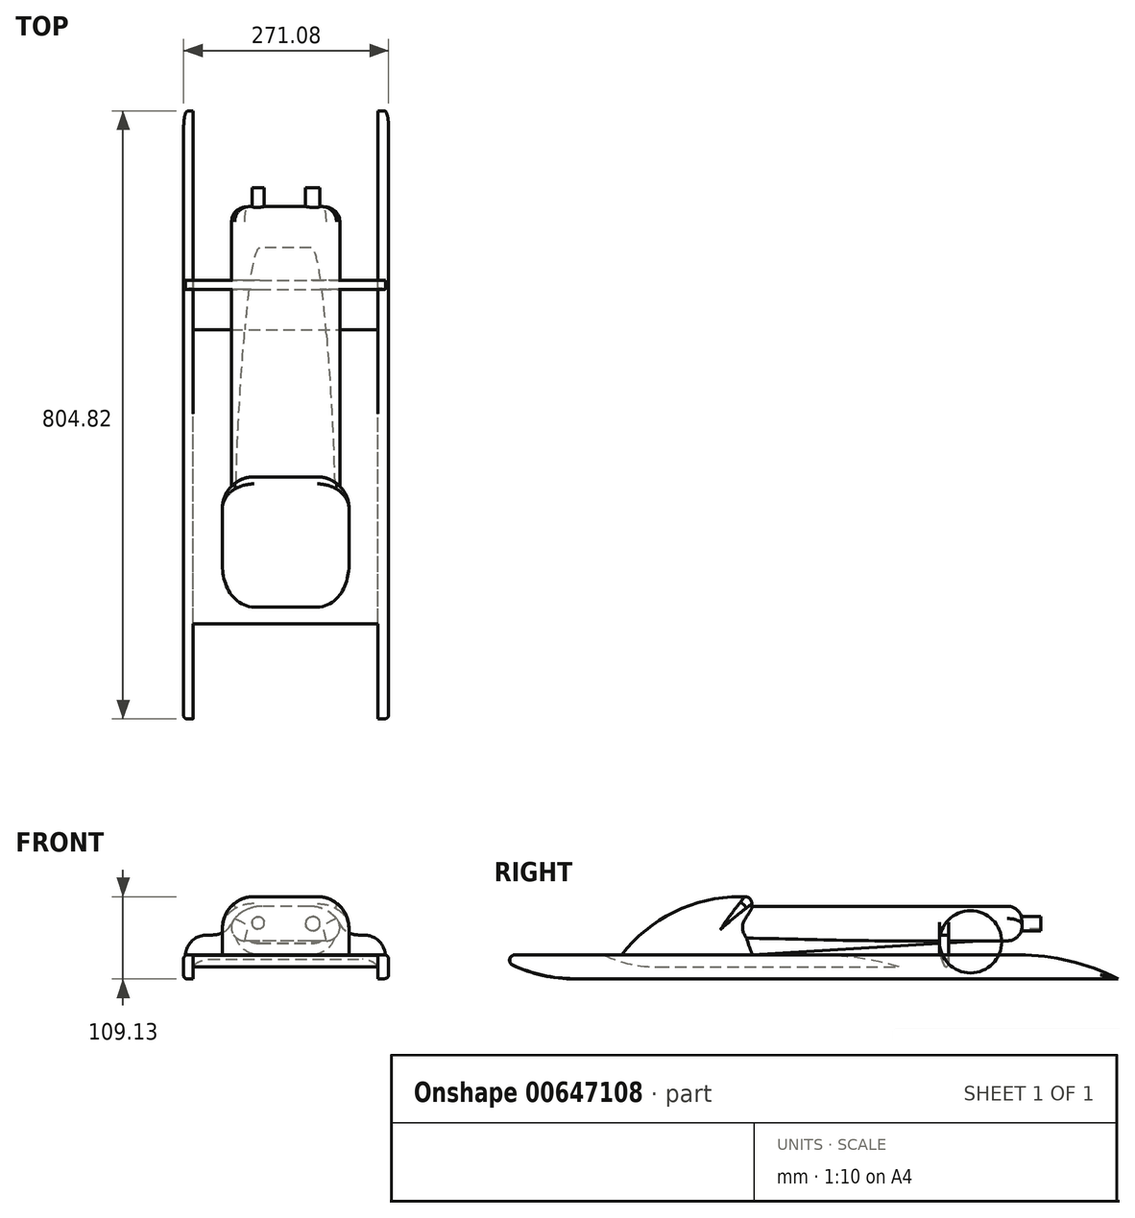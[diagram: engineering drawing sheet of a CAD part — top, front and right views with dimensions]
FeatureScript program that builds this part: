
annotation { "Feature Type Name" : "Feature", "Feature Type Description" : "" }
export const myFeature = defineFeature(function(context is Context, id is Id, definition is map)
    precondition{}
    {
        {
            var Q0;
            Q0=qCreatedBy(makeId("Front.planeOp"),FACE);
            var sketch = newSketch(context, id + "F0", { "sketchPlane" : qUnion([Q0])});
            skLineSegment(sketch, "E0.bottom", {"start": v(-123.74, 0) * mm, "end": v(124.22, 0) * mm});
            skLineSegment(sketch, "E0.top", {"start": v(-123.74, -15.94) * mm, "end": v(124.22, -15.94) * mm});
            skLineSegment(sketch, "E0.left", {"start": v(-123.74, 0) * mm, "end": v(-123.74, -15.94) * mm});
            skLineSegment(sketch, "E0.right", {"start": v(124.22, 0) * mm, "end": v(124.22, -15.94) * mm});
            skSolve(sketch);
        }
        {
            var Q0;
            Q0 = qSketchRegion(id + "F0", true);
            extrude(context, id + "F1", {"entities" : qUnion([Q0]), "endBound" : BoundingType.SYMMETRIC, "depth" : 389.65 * mm, "offsetDistance" : 25.4 * mm});
        }
        {
            var Q0;
            Q0=makeQuery(id+"F1.opExtrude","CAP_EDGE",EDGE,{"disambiguationData":[OSD([sQuery(id+"F0.wireOp",EDGE,"E0.bottom")])],"isStart":true});
            fillet(context, id + "F2", {"entities" : qUnion([Q0]), "radius" : 397.04 * mm, "tangentPropagation" : true, "allowEdgeOverflow" : false});
        }
        {
            var Q0;
            Q0=makeQuery(id+"F1.opExtrude","CAP_EDGE",EDGE,{"disambiguationData":[OSD([sQuery(id+"F0.wireOp",EDGE,"E0.top")])],"isStart":false});
            chamfer(context, id + "F3", {"entities" : qUnion([Q0]), "width" : 15.24 * mm, "tangentPropagation" : true});
        }
        {
            var Q0;
            {var subQ0=sQuery(id+"F0.wireOp",EDGE,"E0.top");Q0=makeQuery(id+"F3.opChamfer","BLEND_EDGE",EDGE,{"blendedFrom":[makeQuery(id+"F1.opExtrude","CAP_EDGE",EDGE,{"disambiguationData":[OSD([subQ0])],"isStart":false}),makeQuery(id+"F1.opExtrude","SWEPT_FACE",FACE,{"disambiguationData":[OSD([subQ0])]})],"blendedInto":[makeQuery(id+"F1.opExtrude","SWEPT_FACE",FACE,{"disambiguationData":[OSD([subQ0])]})]});}
            fillet(context, id + "F4", {"entities" : qUnion([Q0]), "radius" : 170.5 * mm, "tangentPropagation" : true, "allowEdgeOverflow" : false});
        }
        {
            var Q0;
            Q0=qCreatedBy(makeId("Front.planeOp"),FACE);
            var sketch = newSketch(context, id + "F5", { "sketchPlane" : qUnion([Q0])});
            skLineSegment(sketch, "E1.bottom", {"start": v(122.61, 0) * mm, "end": v(136.46, 0) * mm});
            skLineSegment(sketch, "E1.top", {"start": v(122.61, -31.37) * mm, "end": v(136.46, -31.37) * mm});
            skLineSegment(sketch, "E1.left", {"start": v(122.61, 0) * mm, "end": v(122.61, -31.37) * mm});
            skLineSegment(sketch, "E1.right", {"start": v(136.46, 0) * mm, "end": v(136.46, -31.37) * mm});
            skLineSegment(sketch, "E2.bottom", {"start": v(-122.4, 0) * mm, "end": v(-134.62, 0) * mm});
            skLineSegment(sketch, "E2.top", {"start": v(-122.4, -31.9) * mm, "end": v(-134.62, -31.9) * mm});
            skLineSegment(sketch, "E2.left", {"start": v(-122.4, 0) * mm, "end": v(-122.4, -31.9) * mm});
            skLineSegment(sketch, "E2.right", {"start": v(-134.62, 0) * mm, "end": v(-134.62, -31.9) * mm});
            skSolve(sketch);
        }
        {
            var Q0;
            Q0 = qSketchRegion(id + "F5", true);
            extrude(context, id + "F6", {"entities" : qUnion([Q0]), "operationType" : NewBodyOperationType.ADD, "endBound" : BoundingType.SYMMETRIC, "depth" : 680.15 * mm, "offsetDistance" : 25.4 * mm});
        }
        {
            var Q0;
            Q0=makeQuery(id+"F6.opExtrude","CAP_EDGE",EDGE,{"disambiguationData":[OSD([sQuery(id+"F5.wireOp",EDGE,"E1.top")])],"isStart":false});
            var Q1;
            Q1=makeQuery(id+"F6.opExtrude","CAP_EDGE",EDGE,{"disambiguationData":[OSD([sQuery(id+"F5.wireOp",EDGE,"E2.top")])],"isStart":false});
            fillet(context, id + "F7", {"entities" : qUnion([Q0, Q1]), "radius" : 190.44 * mm, "tangentPropagation" : true, "allowEdgeOverflow" : false});
        }
        {
            var Q0;
            Q0=makeQuery(id+"F6.opExtrude","CAP_FACE",FACE,{"disambiguationData":[OSD([sQuery(id+"F5.wireOp",EDGE,"E2.bottom"),sQuery(id+"F5.wireOp",EDGE,"E2.top"),sQuery(id+"F5.wireOp",EDGE,"E2.left"),sQuery(id+"F5.wireOp",EDGE,"E2.right")])],"isStart":true});
            var Q1;
            Q1=makeQuery(id+"F6.opExtrude","CAP_FACE",FACE,{"disambiguationData":[OSD([sQuery(id+"F5.wireOp",EDGE,"E1.bottom"),sQuery(id+"F5.wireOp",EDGE,"E1.top"),sQuery(id+"F5.wireOp",EDGE,"E1.left"),sQuery(id+"F5.wireOp",EDGE,"E1.right")])],"isStart":true});
            extrude(context, id + "F8", {"entities" : qUnion([Q0, Q1]), "operationType" : NewBodyOperationType.ADD, "depth" : 144.15 * mm, "offsetDistance" : 25.4 * mm});
        }
        {
            var Q0;
            Q0=makeQuery(id+"F8.opExtrude","CAP_EDGE",EDGE,{"disambiguationData":[OSD([sQuery(id+"F5.wireOp",EDGE,"E2.bottom")])],"isStart":false});
            var Q1;
            Q1=makeQuery(id+"F8.opExtrude","CAP_EDGE",EDGE,{"disambiguationData":[OSD([sQuery(id+"F5.wireOp",EDGE,"E1.bottom")])],"isStart":false});
            fillet(context, id + "F9", {"entities" : qUnion([Q0, Q1]), "radius" : 288.6 * mm, "tangentPropagation" : true, "allowEdgeOverflow" : false});
        }
        {
            var Q0;
            Q0=qCreatedBy(makeId("Front.planeOp"),FACE);
            var sketch = newSketch(context, id + "F10", { "sketchPlane" : qUnion([Q0])});
            skLineSegment(sketch, "E3.bottom", {"start": v(-83.53, 0) * mm, "end": v(84.18, 0) * mm});
            skLineSegment(sketch, "E3.top", {"start": v(-83.53, 77.23) * mm, "end": v(84.18, 77.23) * mm});
            skLineSegment(sketch, "E3.left", {"start": v(-83.53, 0) * mm, "end": v(-83.53, 77.23) * mm});
            skLineSegment(sketch, "E3.right", {"start": v(84.18, 0) * mm, "end": v(84.18, 77.23) * mm});
            skSolve(sketch);
        }
        {
            var Q0;
            Q0 = qSketchRegion(id + "F10", true);
            extrude(context, id + "F11", {"entities" : qUnion([Q0]), "operationType" : NewBodyOperationType.ADD, "depth" : 172.3 * mm, "offsetDistance" : 25.4 * mm});
        }
        {
            var Q0;
            Q0=makeQuery(id+"F11.opExtrude","CAP_EDGE",EDGE,{"disambiguationData":[OSD([sQuery(id+"F10.wireOp",EDGE,"E3.top")])],"isStart":false});
            fillet(context, id + "F12", {"entities" : qUnion([Q0]), "radius" : 198.08 * mm, "tangentPropagation" : true, "allowEdgeOverflow" : false});
        }
        {
            var Q0;
            Q0=makeQuery(id+"F11.opExtrude","CAP_EDGE",EDGE,{"disambiguationData":[OSD([sQuery(id+"F10.wireOp",EDGE,"E3.top")])],"isStart":true});
            fillet(context, id + "F13", {"entities" : qUnion([Q0]), "radius" : 9.37 * mm, "tangentPropagation" : true, "allowEdgeOverflow" : false});
        }
        {
            var Q0;
            Q0=makeQuery(id+"F7.opFillet","BLEND_EDGE",EDGE,{"blendedFrom":[makeQuery(id+"F6.opExtrude","CAP_EDGE",EDGE,{"disambiguationData":[OSD([sQuery(id+"F5.wireOp",EDGE,"E2.top")])],"isStart":false}),makeQuery(id+"F6.boolean.opBoolean","MERGE",FACE,{"derivedFrom":[makeQuery(id+"F1.opExtrude","SWEPT_FACE",FACE,{"disambiguationData":[OSD([sQuery(id+"F0.wireOp",EDGE,"E0.bottom")])]}),makeQuery(id+"F6.opExtrude","SWEPT_FACE",FACE,{"disambiguationData":[OSD([sQuery(id+"F5.wireOp",EDGE,"E1.bottom")])]}),makeQuery(id+"F6.opExtrude","SWEPT_FACE",FACE,{"disambiguationData":[OSD([sQuery(id+"F5.wireOp",EDGE,"E2.bottom")])]})]})],"blendedInto":[makeQuery(id+"F6.boolean.opBoolean","MERGE",FACE,{"derivedFrom":[makeQuery(id+"F1.opExtrude","SWEPT_FACE",FACE,{"disambiguationData":[OSD([sQuery(id+"F0.wireOp",EDGE,"E0.bottom")])]}),makeQuery(id+"F6.opExtrude","SWEPT_FACE",FACE,{"disambiguationData":[OSD([sQuery(id+"F5.wireOp",EDGE,"E1.bottom")])]}),makeQuery(id+"F6.opExtrude","SWEPT_FACE",FACE,{"disambiguationData":[OSD([sQuery(id+"F5.wireOp",EDGE,"E2.bottom")])]})]})]});
            var Q1;
            Q1=makeQuery(id+"F7.opFillet","BLEND_EDGE",EDGE,{"blendedFrom":[makeQuery(id+"F6.opExtrude","CAP_EDGE",EDGE,{"disambiguationData":[OSD([sQuery(id+"F5.wireOp",EDGE,"E1.top")])],"isStart":false}),makeQuery(id+"F6.boolean.opBoolean","MERGE",FACE,{"derivedFrom":[makeQuery(id+"F1.opExtrude","SWEPT_FACE",FACE,{"disambiguationData":[OSD([sQuery(id+"F0.wireOp",EDGE,"E0.bottom")])]}),makeQuery(id+"F6.opExtrude","SWEPT_FACE",FACE,{"disambiguationData":[OSD([sQuery(id+"F5.wireOp",EDGE,"E1.bottom")])]}),makeQuery(id+"F6.opExtrude","SWEPT_FACE",FACE,{"disambiguationData":[OSD([sQuery(id+"F5.wireOp",EDGE,"E2.bottom")])]})]})],"blendedInto":[makeQuery(id+"F6.boolean.opBoolean","MERGE",FACE,{"derivedFrom":[makeQuery(id+"F1.opExtrude","SWEPT_FACE",FACE,{"disambiguationData":[OSD([sQuery(id+"F0.wireOp",EDGE,"E0.bottom")])]}),makeQuery(id+"F6.opExtrude","SWEPT_FACE",FACE,{"disambiguationData":[OSD([sQuery(id+"F5.wireOp",EDGE,"E1.bottom")])]}),makeQuery(id+"F6.opExtrude","SWEPT_FACE",FACE,{"disambiguationData":[OSD([sQuery(id+"F5.wireOp",EDGE,"E2.bottom")])]})]})]});
            fillet(context, id + "F14", {"entities" : qUnion([Q0, Q1]), "radius" : 7 * mm, "tangentPropagation" : true, "allowEdgeOverflow" : false});
        }
        {
            var Q0;
            Q0=qCreatedBy(makeId("Front.planeOp"),FACE);
            var sketch = newSketch(context, id + "F15", { "sketchPlane" : qUnion([Q0])});
            skLineSegment(sketch, "E4.bottom", {"start": v(79.44, 64.47) * mm, "end": v(-78.92, 64.47) * mm});
            skLineSegment(sketch, "E4.top", {"start": v(79.44, 18.65) * mm, "end": v(-78.92, 18.65) * mm});
            skLineSegment(sketch, "E4.left", {"start": v(79.44, 64.47) * mm, "end": v(79.44, 18.65) * mm});
            skLineSegment(sketch, "E4.right", {"start": v(-78.92, 64.47) * mm, "end": v(-78.92, 18.65) * mm});
            skSolve(sketch);
        }
        {
            var Q0;
            Q0 = qSketchRegion(id + "F15", true);
            extrude(context, id + "F16", {"entities" : qUnion([Q0]), "operationType" : NewBodyOperationType.ADD, "oppositeDirection" : true, "depth" : 357.55 * mm, "offsetDistance" : 25.4 * mm});
        }
        {
            var Q0;
            Q0=qCreatedBy(makeId("Right.planeOp"),FACE);
            var sketch = newSketch(context, id + "F17", { "sketchPlane" : qUnion([Q0])});
            skLineSegment(sketch, "E5", {"start": v(350.7, 21.59) * mm, "end": v(0, 0) * mm});
            skLineSegment(sketch, "E6", {"start": v(0, 0) * mm, "end": v(-0.17, 23.5) * mm});
            skLineSegment(sketch, "E7", {"start": v(-0.17, 23.5) * mm, "end": v(350.7, 21.59) * mm});
            skSolve(sketch);
        }
        {
            var Q0;
            Q0=makeQuery(id+"F17.imprint","IMPRINT",FACE,{"disambiguationData":[TD([[makeQuery(id+"F17.imprint","IMPRINT",EDGE,{"derivedFrom":sQuery(id+"F17.wireOp",EDGE,"E5")}),-1.0]])]});
            extrude(context, id + "F18", {"entities" : qUnion([Q0]), "operationType" : NewBodyOperationType.ADD, "endBound" : BoundingType.SYMMETRIC, "depth" : 133.14 * mm, "offsetDistance" : 25.4 * mm});
        }
        {
            var Q0;
            Q0=makeQuery(id+"F18.opExtrude","CAP_EDGE",EDGE,{"disambiguationData":[OSD([sQuery(id+"F17.wireOp",EDGE,"E5")])],"isStart":false});
            var Q1;
            Q1=makeQuery(id+"F18.opExtrude","CAP_EDGE",EDGE,{"disambiguationData":[OSD([sQuery(id+"F17.wireOp",EDGE,"E5")])],"isStart":true});
            fillet(context, id + "F19", {"entities" : qUnion([Q0, Q1]), "radius" : 32.62 * mm, "tangentPropagation" : true, "allowEdgeOverflow" : false});
        }
        {
            var Q0;
            Q0=makeQuery(id+"F12.opFillet","BLEND_EDGE",EDGE,{"blendedFrom":[makeQuery(id+"F11.opExtrude","CAP_EDGE",EDGE,{"disambiguationData":[OSD([sQuery(id+"F10.wireOp",EDGE,"E3.top")])],"isStart":false}),makeQuery(id+"F11.opExtrude","SWEPT_FACE",FACE,{"disambiguationData":[OSD([sQuery(id+"F10.wireOp",EDGE,"E3.right")])]})],"blendedInto":[makeQuery(id+"F11.opExtrude","SWEPT_FACE",FACE,{"disambiguationData":[OSD([sQuery(id+"F10.wireOp",EDGE,"E3.right")])]})]});
            var Q1;
            Q1=makeQuery(id+"F12.opFillet","BLEND_EDGE",EDGE,{"blendedFrom":[makeQuery(id+"F11.opExtrude","CAP_EDGE",EDGE,{"disambiguationData":[OSD([sQuery(id+"F10.wireOp",EDGE,"E3.top")])],"isStart":false}),makeQuery(id+"F11.opExtrude","SWEPT_FACE",FACE,{"disambiguationData":[OSD([sQuery(id+"F10.wireOp",EDGE,"E3.left")])]})],"blendedInto":[makeQuery(id+"F11.opExtrude","SWEPT_FACE",FACE,{"disambiguationData":[OSD([sQuery(id+"F10.wireOp",EDGE,"E3.left")])]})]});
            fillet(context, id + "F20", {"entities" : qUnion([Q0, Q1]), "radius" : 42.05 * mm, "tangentPropagation" : true, "allowEdgeOverflow" : false});
        }
        {
            var Q0;
            Q0=makeQuery(id+"F16.opExtrude","SWEPT_EDGE",EDGE,{"disambiguationData":[OSD([sQuery(id+"F15.wireOp",EDGE,"E4.bottom"),sQuery(id+"F15.wireOp",EDGE,"E4.right")])]});
            var Q1;
            Q1=makeQuery(id+"F16.opExtrude","SWEPT_EDGE",EDGE,{"disambiguationData":[OSD([sQuery(id+"F15.wireOp",EDGE,"E4.bottom"),sQuery(id+"F15.wireOp",EDGE,"E4.left")])]});
            fillet(context, id + "F21", {"entities" : qUnion([Q0, Q1]), "radius" : 48.04 * mm, "tangentPropagation" : true, "allowEdgeOverflow" : false});
        }
        {
            var Q0;
            Q0=makeQuery(id+"F21.opFillet","BLEND_EDGE",EDGE,{"blendedFrom":[makeQuery(id+"F16.opExtrude","SWEPT_EDGE",EDGE,{"disambiguationData":[OSD([sQuery(id+"F15.wireOp",EDGE,"E4.bottom"),sQuery(id+"F15.wireOp",EDGE,"E4.left")])]}),makeQuery(id+"F16.opExtrude","SWEPT_FACE",FACE,{"disambiguationData":[OSD([sQuery(id+"F15.wireOp",EDGE,"E4.top")])]})],"blendedInto":[makeQuery(id+"F16.opExtrude","SWEPT_FACE",FACE,{"disambiguationData":[OSD([sQuery(id+"F15.wireOp",EDGE,"E4.top")])]})]});
            var Q1;
            Q1=makeQuery(id+"F21.opFillet","BLEND_EDGE",EDGE,{"blendedFrom":[makeQuery(id+"F16.opExtrude","SWEPT_EDGE",EDGE,{"disambiguationData":[OSD([sQuery(id+"F15.wireOp",EDGE,"E4.bottom"),sQuery(id+"F15.wireOp",EDGE,"E4.right")])]}),makeQuery(id+"F16.opExtrude","SWEPT_FACE",FACE,{"disambiguationData":[OSD([sQuery(id+"F15.wireOp",EDGE,"E4.top")])]})],"blendedInto":[makeQuery(id+"F16.opExtrude","SWEPT_FACE",FACE,{"disambiguationData":[OSD([sQuery(id+"F15.wireOp",EDGE,"E4.top")])]})]});
            fillet(context, id + "F22", {"entities" : qUnion([Q0, Q1]), "radius" : 17.76 * mm, "tangentPropagation" : true, "allowEdgeOverflow" : false});
        }
        {
            var Q0;
            Q0=makeQuery(id+"F16.opExtrude","CAP_FACE",FACE,{"disambiguationData":[OSD([sQuery(id+"F15.wireOp",EDGE,"E4.bottom"),sQuery(id+"F15.wireOp",EDGE,"E4.top"),sQuery(id+"F15.wireOp",EDGE,"E4.left"),sQuery(id+"F15.wireOp",EDGE,"E4.right")])],"isStart":false});
            fillet(context, id + "F23", {"entities" : qUnion([Q0]), "radius" : 19.7 * mm, "tangentPropagation" : true, "allowEdgeOverflow" : false});
        }
        {
            var Q0;
            Q0=qCreatedBy(makeId("Right.planeOp"),FACE);
            var sketch = newSketch(context, id + "F24", { "sketchPlane" : qUnion([Q0])});
            skLineSegment(sketch, "E8.bottom", {"start": v(260.18, 26.41) * mm, "end": v(248.12, 26.41) * mm});
            skLineSegment(sketch, "E8.top", {"start": v(260.18, -11.71) * mm, "end": v(248.12, -11.71) * mm});
            skLineSegment(sketch, "E8.left", {"start": v(260.18, 26.41) * mm, "end": v(260.18, -11.71) * mm});
            skLineSegment(sketch, "E8.right", {"start": v(248.12, 26.41) * mm, "end": v(248.12, -11.71) * mm});
            skSolve(sketch);
        }
        {
            var Q0;
            Q0 = qSketchRegion(id + "F24", true);
            extrude(context, id + "F25", {"entities" : qUnion([Q0]), "operationType" : NewBodyOperationType.ADD, "endBound" : BoundingType.SYMMETRIC, "depth" : 264.57 * mm, "offsetDistance" : 25.4 * mm});
        }
        {
            var Q0;
            Q0=makeQuery(id+"F25.opExtrude","CAP_EDGE",EDGE,{"disambiguationData":[OSD([sQuery(id+"F24.wireOp",EDGE,"E8.bottom")])],"isStart":true});
            var Q1;
            Q1=makeQuery(id+"F25.boolean.opBoolean","INTERSECT",EDGE,{"derivedFrom":[makeQuery(id+"F22.opFillet","BLEND_FACE",FACE,{"disambiguationData":[OSD([sQuery(id+"F15.wireOp",EDGE,"E4.bottom"),sQuery(id+"F15.wireOp",EDGE,"E4.top"),sQuery(id+"F15.wireOp",EDGE,"E4.right")])]}),makeQuery(id+"F25.opExtrude","SWEPT_FACE",FACE,{"disambiguationData":[OSD([sQuery(id+"F24.wireOp",EDGE,"E8.bottom")])]})]});
            var Q2;
            Q2=makeQuery(id+"F25.opExtrude","CAP_EDGE",EDGE,{"disambiguationData":[OSD([sQuery(id+"F24.wireOp",EDGE,"E8.bottom")])],"isStart":false});
            var Q3;
            Q3=makeQuery(id+"F25.boolean.opBoolean","INTERSECT",EDGE,{"derivedFrom":[makeQuery(id+"F22.opFillet","BLEND_FACE",FACE,{"disambiguationData":[OSD([sQuery(id+"F15.wireOp",EDGE,"E4.bottom"),sQuery(id+"F15.wireOp",EDGE,"E4.top"),sQuery(id+"F15.wireOp",EDGE,"E4.left")])]}),makeQuery(id+"F25.opExtrude","SWEPT_FACE",FACE,{"disambiguationData":[OSD([sQuery(id+"F24.wireOp",EDGE,"E8.bottom")])]})]});
            fillet(context, id + "F26", {"entities" : qUnion([Q0, Q1, Q2, Q3]), "radius" : 28.48 * mm, "tangentPropagation" : true, "allowEdgeOverflow" : false});
        }
        {
            var Q0;
            {var subQ0=sQuery(id+"F5.wireOp",EDGE,"E1.left");Q0=makeQuery(id+"F25.boolean.opBoolean","INTERSECT",EDGE,{"derivedFrom":[makeQuery(id+"F8.boolean.opBoolean","MERGE",FACE,{"derivedFrom":[makeQuery(id+"F6.opExtrude","SWEPT_FACE",FACE,{"disambiguationData":[OSD([subQ0])]}),makeQuery(id+"F8.opExtrude","SWEPT_FACE",FACE,{"disambiguationData":[OSD([subQ0])]})]}),makeQuery(id+"F25.opExtrude","SWEPT_FACE",FACE,{"disambiguationData":[OSD([sQuery(id+"F24.wireOp",EDGE,"E8.top")])]})]});}
            var Q1;
            {var subQ0=sQuery(id+"F5.wireOp",EDGE,"E2.left");Q1=makeQuery(id+"F25.boolean.opBoolean","INTERSECT",EDGE,{"derivedFrom":[makeQuery(id+"F8.boolean.opBoolean","MERGE",FACE,{"derivedFrom":[makeQuery(id+"F6.opExtrude","SWEPT_FACE",FACE,{"disambiguationData":[OSD([subQ0])]}),makeQuery(id+"F8.opExtrude","SWEPT_FACE",FACE,{"disambiguationData":[OSD([subQ0])]})]}),makeQuery(id+"F25.opExtrude","SWEPT_FACE",FACE,{"disambiguationData":[OSD([sQuery(id+"F24.wireOp",EDGE,"E8.top")])]})]});}
            fillet(context, id + "F27", {"entities" : qUnion([Q0, Q1]), "radius" : 20.53 * mm, "tangentPropagation" : true, "allowEdgeOverflow" : false});
        }
        {
            var Q0;
            {var subQ0=sQuery(id+"F5.wireOp",EDGE,"E2.left");Q0=makeQuery(id+"F27.opFillet","BLEND_EDGE",EDGE,{"blendedFrom":[makeQuery(id+"F25.boolean.opBoolean","INTERSECT",EDGE,{"derivedFrom":[makeQuery(id+"F8.boolean.opBoolean","MERGE",FACE,{"derivedFrom":[makeQuery(id+"F6.opExtrude","SWEPT_FACE",FACE,{"disambiguationData":[OSD([subQ0])]}),makeQuery(id+"F8.opExtrude","SWEPT_FACE",FACE,{"disambiguationData":[OSD([subQ0])]})]}),makeQuery(id+"F25.opExtrude","SWEPT_FACE",FACE,{"disambiguationData":[OSD([sQuery(id+"F24.wireOp",EDGE,"E8.top")])]})]}),makeQuery(id+"F25.opExtrude","SWEPT_FACE",FACE,{"disambiguationData":[OSD([sQuery(id+"F24.wireOp",EDGE,"E8.right")])]})],"blendedInto":[makeQuery(id+"F25.opExtrude","SWEPT_FACE",FACE,{"disambiguationData":[OSD([sQuery(id+"F24.wireOp",EDGE,"E8.right")])]})]});}
            var Q1;
            Q1=makeQuery(id+"F25.opExtrude","SWEPT_EDGE",EDGE,{"disambiguationData":[OSD([sQuery(id+"F24.wireOp",EDGE,"E8.top"),sQuery(id+"F24.wireOp",EDGE,"E8.right")])]});
            var Q2;
            {var subQ0=sQuery(id+"F5.wireOp",EDGE,"E1.left");Q2=makeQuery(id+"F27.opFillet","BLEND_EDGE",EDGE,{"blendedFrom":[makeQuery(id+"F25.boolean.opBoolean","INTERSECT",EDGE,{"derivedFrom":[makeQuery(id+"F8.boolean.opBoolean","MERGE",FACE,{"derivedFrom":[makeQuery(id+"F6.opExtrude","SWEPT_FACE",FACE,{"disambiguationData":[OSD([subQ0])]}),makeQuery(id+"F8.opExtrude","SWEPT_FACE",FACE,{"disambiguationData":[OSD([subQ0])]})]}),makeQuery(id+"F25.opExtrude","SWEPT_FACE",FACE,{"disambiguationData":[OSD([sQuery(id+"F24.wireOp",EDGE,"E8.top")])]})]}),makeQuery(id+"F25.opExtrude","SWEPT_FACE",FACE,{"disambiguationData":[OSD([sQuery(id+"F24.wireOp",EDGE,"E8.right")])]})],"blendedInto":[makeQuery(id+"F25.opExtrude","SWEPT_FACE",FACE,{"disambiguationData":[OSD([sQuery(id+"F24.wireOp",EDGE,"E8.right")])]})]});}
            fillet(context, id + "F28", {"entities" : qUnion([Q0, Q1, Q2]), "radius" : 41.19 * mm, "tangentPropagation" : true, "allowEdgeOverflow" : false});
        }
        {
            var Q0;
            Q0=makeQuery(id+"F28.opFillet","BLEND_EDGE",EDGE,{"blendedFrom":[makeQuery(id+"F25.opExtrude","SWEPT_EDGE",EDGE,{"disambiguationData":[OSD([sQuery(id+"F24.wireOp",EDGE,"E8.top"),sQuery(id+"F24.wireOp",EDGE,"E8.right")])]}),makeQuery(id+"F25.opExtrude","SWEPT_FACE",FACE,{"disambiguationData":[OSD([sQuery(id+"F24.wireOp",EDGE,"E8.left")])]})],"blendedInto":[makeQuery(id+"F25.opExtrude","SWEPT_FACE",FACE,{"disambiguationData":[OSD([sQuery(id+"F24.wireOp",EDGE,"E8.left")])]})]});
            var Q1;
            {var subQ0=sQuery(id+"F5.wireOp",EDGE,"E1.left");Q1=makeQuery(id+"F28.opFillet","BLEND_EDGE",EDGE,{"blendedFrom":[makeQuery(id+"F27.opFillet","BLEND_EDGE",EDGE,{"blendedFrom":[makeQuery(id+"F25.boolean.opBoolean","INTERSECT",EDGE,{"derivedFrom":[makeQuery(id+"F8.boolean.opBoolean","MERGE",FACE,{"derivedFrom":[makeQuery(id+"F6.opExtrude","SWEPT_FACE",FACE,{"disambiguationData":[OSD([subQ0])]}),makeQuery(id+"F8.opExtrude","SWEPT_FACE",FACE,{"disambiguationData":[OSD([subQ0])]})]}),makeQuery(id+"F25.opExtrude","SWEPT_FACE",FACE,{"disambiguationData":[OSD([sQuery(id+"F24.wireOp",EDGE,"E8.top")])]})]}),makeQuery(id+"F25.opExtrude","SWEPT_FACE",FACE,{"disambiguationData":[OSD([sQuery(id+"F24.wireOp",EDGE,"E8.right")])]})],"blendedInto":[makeQuery(id+"F25.opExtrude","SWEPT_FACE",FACE,{"disambiguationData":[OSD([sQuery(id+"F24.wireOp",EDGE,"E8.right")])]})]}),makeQuery(id+"F25.opExtrude","SWEPT_FACE",FACE,{"disambiguationData":[OSD([sQuery(id+"F24.wireOp",EDGE,"E8.left")])]})],"blendedInto":[makeQuery(id+"F25.opExtrude","SWEPT_FACE",FACE,{"disambiguationData":[OSD([sQuery(id+"F24.wireOp",EDGE,"E8.left")])]})]});}
            fillet(context, id + "F29", {"entities" : qUnion([Q0, Q1]), "radius" : 3.14 * mm, "tangentPropagation" : true, "allowEdgeOverflow" : false});
        }
        {
            var Q0;
            Q0=qCreatedBy(makeId("Front.planeOp"),FACE);
            var sketch = newSketch(context, id + "F30", { "sketchPlane" : qUnion([Q0])});
            skCircle(sketch, "E9", {"center": v(36.24, 41.31) * mm, "radius": 9.54 * mm});
            skCircle(sketch, "E10", {"center": v(-36.12, 42.3) * mm, "radius": 8.19 * mm});
            skSolve(sketch);
        }
        {
            var Q0;
            Q0 = qSketchRegion(id + "F30", true);
            extrude(context, id + "F31", {"entities" : qUnion([Q0]), "operationType" : NewBodyOperationType.ADD, "oppositeDirection" : true, "depth" : 382.47 * mm, "offsetDistance" : 25.4 * mm});
        }
        {
            var Q0;
            Q0=qCreatedBy(makeId("Front.planeOp"),FACE);
            var sketch = newSketch(context, id + "F32", { "sketchPlane" : qUnion([Q0])});
            skCircle(sketch, "E11", {"center": v(36.18, 41.12) * mm, "radius": 6.17 * mm});
            skCircle(sketch, "E12", {"center": v(-36.03, 42.47) * mm, "radius": 5.47 * mm});
            skSolve(sketch);
        }
        {
            var Q0;
            Q0=sQuery(id+"F32.wireOp",EDGE,"E11");
            var Q1;
            Q1=sQuery(id+"F32.wireOp",EDGE,"E12");
            extrude(context, id + "F33", {"bodyType" : ToolBodyType.SURFACE, "surfaceEntities" : qUnion([Q0, Q1]), "oppositeDirection" : true, "depth" : 417.23 * mm, "offsetDistance" : 25.4 * mm});
        }
        {
            var Q0;
            {var subQ0=sQuery(id+"F5.wireOp",EDGE,"E1.right");var subQ1=sQuery(id+"F5.wireOp",EDGE,"E1.top");Q0=makeQuery(id+"F8.boolean.opBoolean","MERGE",EDGE,{"derivedFrom":[makeQuery(id+"F6.opExtrude","SWEPT_EDGE",EDGE,{"disambiguationData":[OSD([subQ1,subQ0])]}),makeQuery(id+"F8.opExtrude","SWEPT_EDGE",EDGE,{"disambiguationData":[OSD([subQ1,subQ0])]})]});}
            var Q1;
            {var subQ0=sQuery(id+"F5.wireOp",EDGE,"E2.right");var subQ1=sQuery(id+"F5.wireOp",EDGE,"E2.top");Q1=makeQuery(id+"F8.boolean.opBoolean","MERGE",EDGE,{"derivedFrom":[makeQuery(id+"F6.opExtrude","SWEPT_EDGE",EDGE,{"disambiguationData":[OSD([subQ1,subQ0])]}),makeQuery(id+"F8.opExtrude","SWEPT_EDGE",EDGE,{"disambiguationData":[OSD([subQ1,subQ0])]})]});}
            fillet(context, id + "F34", {"entities" : qUnion([Q0, Q1]), "radius" : 5.08 * mm, "tangentPropagation" : true, "allowEdgeOverflow" : false});
        }
    });
